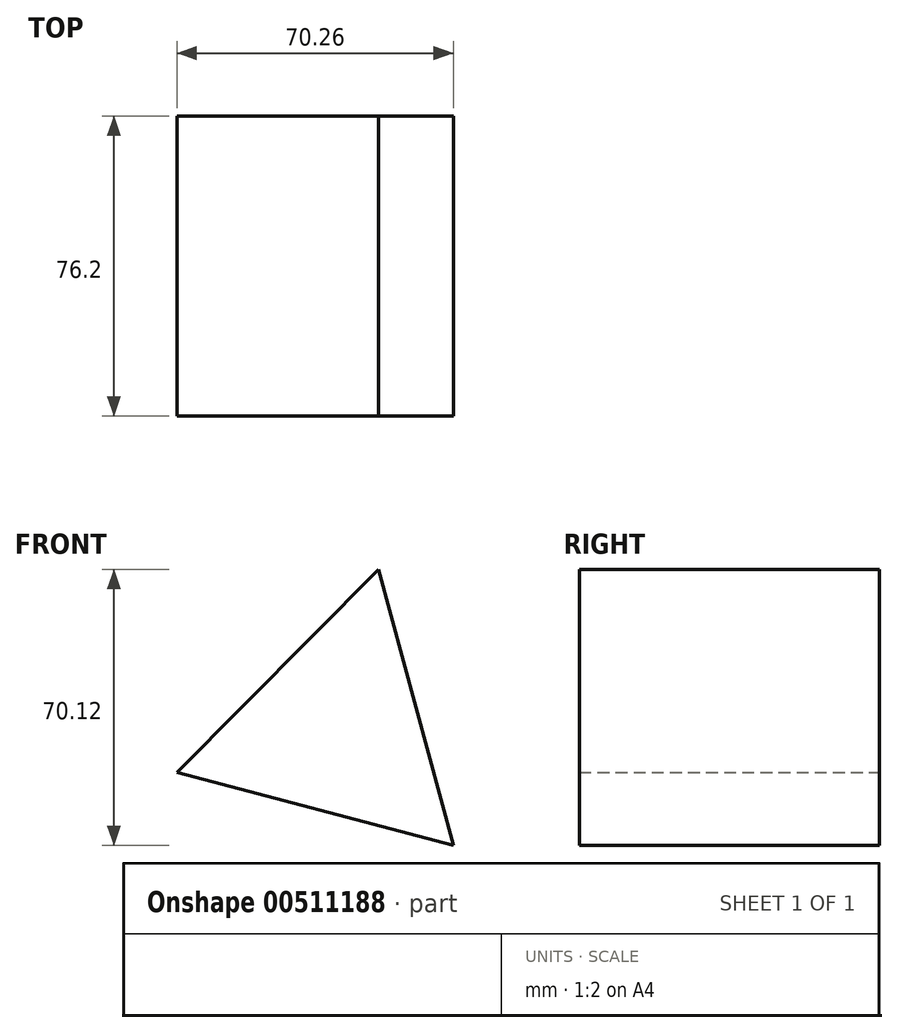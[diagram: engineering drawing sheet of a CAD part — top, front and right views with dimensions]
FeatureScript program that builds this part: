
annotation { "Feature Type Name" : "Feature", "Feature Type Description" : "" }
export const myFeature = defineFeature(function(context is Context, id is Id, definition is map)
    precondition{}
    {
        {
            var Q0;
            Q0=qCreatedBy(makeId("Front.planeOp"),FACE);
            var sketch = newSketch(context, id + "F0", { "sketchPlane" : qUnion([Q0])});
            skCircle(sketch, "E0.cCircle", {"center": v(0, 0) * mm, "radius": 41.96 * mm, "construction": true});
            skLineSegment(sketch, "E0.0", {"start": v(10.7, 40.57) * mm, "end": v(29.78, -29.55) * mm});
            skLineSegment(sketch, "E0.1", {"start": v(29.78, -29.55) * mm, "end": v(-40.48, -11.02) * mm});
            skLineSegment(sketch, "E0.2", {"start": v(-40.48, -11.02) * mm, "end": v(10.7, 40.57) * mm});
            skSolve(sketch);
        }
        {
            var Q0;
            Q0 = qSketchRegion(id + "F0", true);
            extrude(context, id + "F1", {"entities" : qUnion([Q0]), "depth" : 76.2 * mm});
        }
    });
